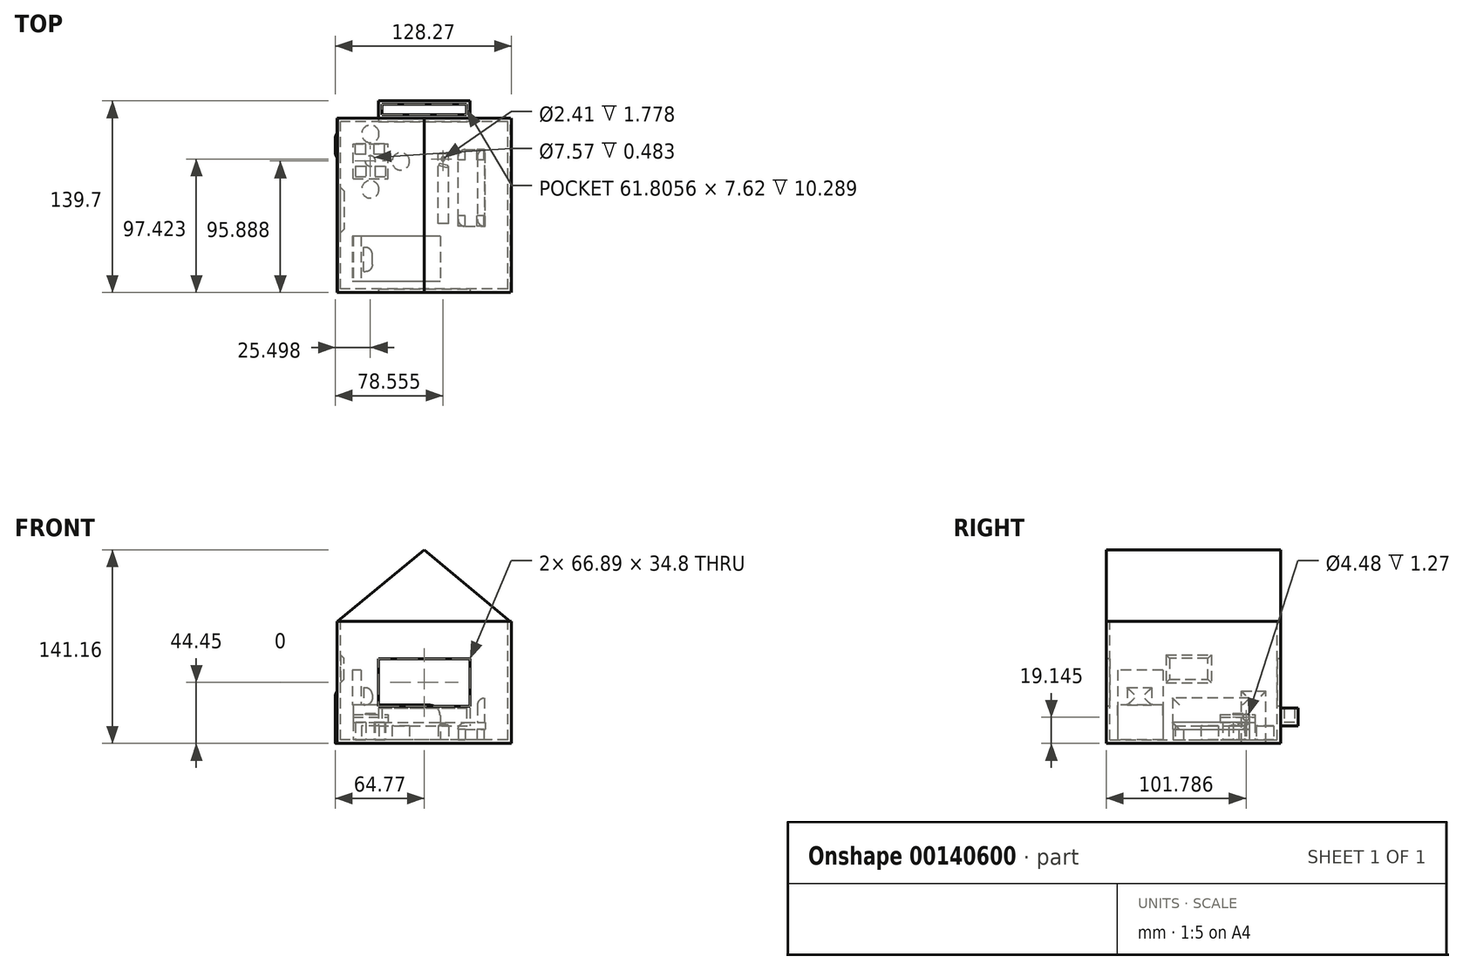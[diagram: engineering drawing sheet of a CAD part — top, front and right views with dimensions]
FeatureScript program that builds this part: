
annotation { "Feature Type Name" : "Feature", "Feature Type Description" : "" }
export const myFeature = defineFeature(function(context is Context, id is Id, definition is map)
    precondition{}
    {
        {
            var Q0;
            Q0=qCreatedBy(makeId("Front.planeOp"),FACE);
            var sketch = newSketch(context, id + "F0", { "sketchPlane" : qUnion([Q0])});
            skLineSegment(sketch, "E0.bottom", {"start": v(63.5, -44.45) * mm, "end": v(-63.5, -44.45) * mm});
            skLineSegment(sketch, "E0.top", {"start": v(63.5, 44.45) * mm, "end": v(-63.5, 44.45) * mm});
            skLineSegment(sketch, "E0.left", {"start": v(63.5, -44.45) * mm, "end": v(63.5, 44.45) * mm});
            skLineSegment(sketch, "E0.right", {"start": v(-63.5, -44.45) * mm, "end": v(-63.5, 44.45) * mm});
            skPoint(sketch, "E0.middle", {"position": v(0, 0) * mm});
            skSolve(sketch);
        }
        {
            var Q0;
            Q0=makeQuery(id+"F0.imprint","IMPRINT",FACE,{"disambiguationData":[TD([[makeQuery(id+"F0.imprint","IMPRINT",EDGE,{"derivedFrom":sQuery(id+"F0.wireOp",EDGE,"E0.bottom")}),-1.0]])]});
            extrude(context, id + "F1", {"entities" : qUnion([Q0]), "depth" : 127 * mm});
        }
        {
            var Q0;
            Q0=makeQuery(id+"F1.opExtrude","SWEPT_FACE",FACE,{"disambiguationData":[OSD([sQuery(id+"F0.wireOp",EDGE,"E0.top")])]});
            shell(context, id + "F2", {"entities" : qUnion([Q0]), "thickness" : 2.54 * mm});
        }
        {
            var Q0;
            Q0=makeQuery(id+"F2.opShell","OFFSET_FACE",FACE,{"disambiguationData":[OSD([sQuery(id+"F0.wireOp",EDGE,"E0.bottom")])]});
            var sketch = newSketch(context, id + "F3", { "sketchPlane" : qUnion([Q0])});
            skLineSegment(sketch, "E1.bottom", {"start": v(-42.46, -26.31) * mm, "end": v(-50.08, -26.31) * mm});
            skLineSegment(sketch, "E1.top", {"start": v(-42.46, -18.7) * mm, "end": v(-50.08, -18.7) * mm});
            skLineSegment(sketch, "E1.left", {"start": v(-42.46, -26.31) * mm, "end": v(-42.46, -18.7) * mm});
            skLineSegment(sketch, "E1.right", {"start": v(-50.08, -26.31) * mm, "end": v(-50.08, -18.7) * mm});
            skPoint(sketch, "E1.middle", {"position": v(-46.27, -22.5) * mm});
            skLineSegment(sketch, "E2.bottom", {"start": v(-28.9, -26.31) * mm, "end": v(-36.51, -26.31) * mm});
            skLineSegment(sketch, "E2.top", {"start": v(-28.9, -18.7) * mm, "end": v(-36.51, -18.7) * mm});
            skLineSegment(sketch, "E2.left", {"start": v(-28.9, -26.31) * mm, "end": v(-28.9, -18.7) * mm});
            skLineSegment(sketch, "E2.right", {"start": v(-36.51, -26.31) * mm, "end": v(-36.51, -18.7) * mm});
            skPoint(sketch, "E2.middle", {"position": v(-32.7, -22.5) * mm});
            skLineSegment(sketch, "E3.bottom", {"start": v(-50.08, -34.68) * mm, "end": v(-42.46, -34.68) * mm});
            skLineSegment(sketch, "E3.top", {"start": v(-50.08, -42.3) * mm, "end": v(-42.46, -42.3) * mm});
            skLineSegment(sketch, "E3.left", {"start": v(-50.08, -34.68) * mm, "end": v(-50.08, -42.3) * mm});
            skLineSegment(sketch, "E3.right", {"start": v(-42.46, -34.68) * mm, "end": v(-42.46, -42.3) * mm});
            skPoint(sketch, "E3.middle", {"position": v(-46.27, -38.5) * mm});
            skLineSegment(sketch, "E4.bottom", {"start": v(-35.96, -34.68) * mm, "end": v(-28.34, -34.68) * mm});
            skLineSegment(sketch, "E4.top", {"start": v(-35.96, -42.3) * mm, "end": v(-28.34, -42.3) * mm});
            skLineSegment(sketch, "E4.left", {"start": v(-35.96, -34.68) * mm, "end": v(-35.96, -42.3) * mm});
            skLineSegment(sketch, "E4.right", {"start": v(-28.34, -34.68) * mm, "end": v(-28.34, -42.3) * mm});
            skPoint(sketch, "E4.middle", {"position": v(-32.15, -38.5) * mm});
            skPoint(sketch, "E4.cornerSnap0", {"position": v(-46.27, -34.68) * mm});
            skSolve(sketch);
        }
        {
            var Q0;
            Q0=makeQuery(id+"F3.imprint","IMPRINT",FACE,{"disambiguationData":[TD([[makeQuery(id+"F3.imprint","IMPRINT",EDGE,{"derivedFrom":sQuery(id+"F3.wireOp",EDGE,"E1.bottom")}),-1.0]])]});
            var Q1;
            Q1=makeQuery(id+"F3.imprint","IMPRINT",FACE,{"disambiguationData":[TD([[makeQuery(id+"F3.imprint","IMPRINT",EDGE,{"derivedFrom":sQuery(id+"F3.wireOp",EDGE,"E2.bottom")}),-1.0]])]});
            var Q2;
            Q2=makeQuery(id+"F3.imprint","IMPRINT",FACE,{"disambiguationData":[TD([[makeQuery(id+"F3.imprint","IMPRINT",EDGE,{"derivedFrom":sQuery(id+"F3.wireOp",EDGE,"E4.bottom")}),-1.0]])]});
            var Q3;
            Q3=makeQuery(id+"F3.imprint","IMPRINT",FACE,{"disambiguationData":[TD([[makeQuery(id+"F3.imprint","IMPRINT",EDGE,{"derivedFrom":sQuery(id+"F3.wireOp",EDGE,"E3.bottom")}),-1.0]])]});
            extrude(context, id + "F4", {"entities" : qUnion([Q0, Q1, Q2, Q3]), "operationType" : NewBodyOperationType.ADD, "depth" : 12.7 * mm});
        }
        {
            var Q0;
            Q0=makeQuery(id+"F4.opExtrude","CAP_FACE",FACE,{"disambiguationData":[OSD([sQuery(id+"F3.wireOp",EDGE,"E1.bottom"),sQuery(id+"F3.wireOp",EDGE,"E1.top"),sQuery(id+"F3.wireOp",EDGE,"E1.left"),sQuery(id+"F3.wireOp",EDGE,"E1.right")])],"isStart":false});
            var sketch = newSketch(context, id + "F5", { "sketchPlane" : qUnion([Q0])});
            skLineSegment(sketch, "E5.bottom", {"start": v(-51.85, -44.1) * mm, "end": v(-26.45, -44.1) * mm});
            skLineSegment(sketch, "E5.top", {"start": v(-51.85, -18.7) * mm, "end": v(-26.45, -18.7) * mm});
            skLineSegment(sketch, "E5.left", {"start": v(-51.85, -44.1) * mm, "end": v(-51.85, -18.7) * mm});
            skLineSegment(sketch, "E5.right", {"start": v(-26.45, -44.1) * mm, "end": v(-26.45, -18.7) * mm});
            skSolve(sketch);
        }
        {
            var Q0;
            Q0 = qSketchRegion(id + "F5", true);
            extrude(context, id + "F6", {"entities" : qUnion([Q0]), "depth" : 3.8 * mm});
        }
        {
            var Q0;
            Q0=makeQuery(id+"F1.opExtrude","CAP_FACE",FACE,{"disambiguationData":[OSD([sQuery(id+"F0.wireOp",EDGE,"E0.bottom"),sQuery(id+"F0.wireOp",EDGE,"E0.top"),sQuery(id+"F0.wireOp",EDGE,"E0.left"),sQuery(id+"F0.wireOp",EDGE,"E0.right")])],"isStart":false});
            var sketch = newSketch(context, id + "F7", { "sketchPlane" : qUnion([Q0])});
            skLineSegment(sketch, "E6.bottom", {"start": v(-33.44, 17.4) * mm, "end": v(33.44, 17.4) * mm});
            skLineSegment(sketch, "E6.top", {"start": v(-33.44, -17.4) * mm, "end": v(33.44, -17.4) * mm});
            skLineSegment(sketch, "E6.left", {"start": v(-33.44, 17.4) * mm, "end": v(-33.44, -17.4) * mm});
            skLineSegment(sketch, "E6.right", {"start": v(33.44, 17.4) * mm, "end": v(33.44, -17.4) * mm});
            skPoint(sketch, "E6.middle", {"position": v(0, 0) * mm});
            skSolve(sketch);
        }
        {
            var Q0;
            Q0 = qSketchRegion(id + "F7", true);
            extrude(context, id + "F8", {"entities" : qUnion([Q0]), "operationType" : NewBodyOperationType.REMOVE, "oppositeDirection" : true, "depth" : 381 * mm});
        }
        {
            var Q0;
            Q0=makeQuery(id+"F1.opExtrude","SWEPT_FACE",FACE,{"disambiguationData":[OSD([sQuery(id+"F0.wireOp",EDGE,"E0.right")])]});
            var sketch = newSketch(context, id + "F9", { "sketchPlane" : qUnion([Q0])});
            skLineSegment(sketch, "E7.bottom", {"start": v(28.62, -44.45) * mm, "end": v(10.84, -44.45) * mm});
            skLineSegment(sketch, "E7.top", {"start": v(28.62, -6.35) * mm, "end": v(10.84, -6.35) * mm});
            skLineSegment(sketch, "E7.left", {"start": v(28.62, -44.45) * mm, "end": v(28.62, -6.35) * mm});
            skLineSegment(sketch, "E7.right", {"start": v(10.84, -44.45) * mm, "end": v(10.84, -6.35) * mm});
            skPoint(sketch, "E7.middle", {"position": v(19.73, -25.4) * mm});
            skCircle(sketch, "E8", {"center": v(25.21, -25.3) * mm, "radius": 2.24 * mm});
            skSolve(sketch);
        }
        {
            var Q0;
            Q0=makeQuery(id+"F9.imprint","IMPRINT",FACE,{"disambiguationData":[TD([[makeQuery(id+"F9.imprint","IMPRINT",EDGE,{"derivedFrom":sQuery(id+"F9.wireOp",EDGE,"E7.bottom")}),-1.0]])]});
            extrude(context, id + "F10", {"entities" : qUnion([Q0]), "operationType" : NewBodyOperationType.ADD, "depth" : 1.27 * mm});
        }
        {
            var Q0;
            Q0=sQuery(id+"F9.wireOp",EDGE,"E8");
            extrude(context, id + "F11", {"bodyType" : ToolBodyType.SURFACE, "surfaceEntities" : qUnion([Q0]), "depth" : 2.03 * mm});
        }
        {
            var Q0;
            Q0=qCreatedBy(makeId("Front.planeOp"),FACE);
            var sketch = newSketch(context, id + "F12", { "sketchPlane" : qUnion([Q0])});
            skLineSegment(sketch, "E9", {"start": v(-63.16, 44.71) * mm, "end": v(0, 96.7) * mm});
            skLineSegment(sketch, "E10", {"start": v(0, 96.7) * mm, "end": v(62.8, 44.28) * mm});
            skLineSegment(sketch, "E11", {"start": v(62.8, 44.28) * mm, "end": v(-63.16, 44.71) * mm});
            skSolve(sketch);
        }
        {
            var Q0;
            Q0=makeQuery(id+"F12.imprint","IMPRINT",FACE,{"disambiguationData":[TD([[makeQuery(id+"F12.imprint","IMPRINT",EDGE,{"derivedFrom":sQuery(id+"F12.wireOp",EDGE,"E9")}),-1.0]])]});
            extrude(context, id + "F13", {"entities" : qUnion([Q0]), "depth" : 127 * mm});
        }
        {
            var Q0;
            Q0=makeQuery(id+"F2.opShell","OFFSET_FACE",FACE,{"disambiguationData":[OSD([sQuery(id+"F0.wireOp",EDGE,"E0.bottom")])]});
            var sketch = newSketch(context, id + "F14", { "sketchPlane" : qUnion([Q0])});
            skLineSegment(sketch, "E12.bottom", {"start": v(29.76, -30.39) * mm, "end": v(24.68, -30.39) * mm});
            skLineSegment(sketch, "E12.top", {"start": v(29.76, -22.77) * mm, "end": v(24.68, -22.77) * mm});
            skLineSegment(sketch, "E12.left", {"start": v(29.76, -30.39) * mm, "end": v(29.76, -22.77) * mm});
            skLineSegment(sketch, "E12.right", {"start": v(24.68, -30.39) * mm, "end": v(24.68, -22.77) * mm});
            skPoint(sketch, "E12.middle", {"position": v(27.22, -26.58) * mm});
            skLineSegment(sketch, "E13.bottom", {"start": v(43.59, -30.39) * mm, "end": v(38.5, -30.39) * mm});
            skLineSegment(sketch, "E13.top", {"start": v(43.59, -22.77) * mm, "end": v(38.5, -22.77) * mm});
            skLineSegment(sketch, "E13.left", {"start": v(43.59, -30.39) * mm, "end": v(43.59, -22.77) * mm});
            skLineSegment(sketch, "E13.right", {"start": v(38.5, -30.39) * mm, "end": v(38.5, -22.77) * mm});
            skPoint(sketch, "E13.middle", {"position": v(41.05, -26.58) * mm});
            skPoint(sketch, "E13.middle.positionSnap0", {"position": v(29.76, -26.58) * mm});
            skPoint(sketch, "E13.centerSnap0", {"position": v(29.76, -26.58) * mm});
            skLineSegment(sketch, "E14.bottom", {"start": v(43.59, -78.48) * mm, "end": v(38.5, -78.48) * mm});
            skLineSegment(sketch, "E14.top", {"start": v(43.59, -70.86) * mm, "end": v(38.5, -70.86) * mm});
            skLineSegment(sketch, "E14.left", {"start": v(43.59, -78.48) * mm, "end": v(43.59, -70.86) * mm});
            skLineSegment(sketch, "E14.right", {"start": v(38.5, -78.48) * mm, "end": v(38.5, -70.86) * mm});
            skPoint(sketch, "E14.middle", {"position": v(41.05, -74.67) * mm});
            skPoint(sketch, "E14.middle.positionSnap0", {"position": v(41.05, -30.39) * mm});
            skPoint(sketch, "E14.centerSnap0", {"position": v(41.05, -30.39) * mm});
            skLineSegment(sketch, "E15.bottom", {"start": v(29.76, -78.48) * mm, "end": v(24.68, -78.48) * mm});
            skLineSegment(sketch, "E15.top", {"start": v(29.76, -70.86) * mm, "end": v(24.68, -70.86) * mm});
            skLineSegment(sketch, "E15.left", {"start": v(29.76, -78.48) * mm, "end": v(29.76, -70.86) * mm});
            skLineSegment(sketch, "E15.right", {"start": v(24.68, -78.48) * mm, "end": v(24.68, -70.86) * mm});
            skPoint(sketch, "E15.middle", {"position": v(27.22, -74.67) * mm});
            skPoint(sketch, "E15.middle.positionSnap0", {"position": v(27.22, -30.39) * mm});
            skPoint(sketch, "E15.middle.positionSnap1", {"position": v(38.5, -74.67) * mm});
            skPoint(sketch, "E15.centerSnap0", {"position": v(27.22, -30.39) * mm});
            skPoint(sketch, "E15.centerSnap1", {"position": v(38.5, -74.67) * mm});
            skSolve(sketch);
        }
        {
            var Q0;
            Q0 = qSketchRegion(id + "F14", true);
            extrude(context, id + "F15", {"entities" : qUnion([Q0]), "operationType" : NewBodyOperationType.ADD, "depth" : 7.62 * mm});
        }
        {
            var Q0;
            Q0=makeQuery(id+"F15.opExtrude","CAP_FACE",FACE,{"disambiguationData":[OSD([sQuery(id+"F14.wireOp",EDGE,"E12.bottom"),sQuery(id+"F14.wireOp",EDGE,"E12.top"),sQuery(id+"F14.wireOp",EDGE,"E12.left"),sQuery(id+"F14.wireOp",EDGE,"E12.right")])],"isStart":false});
            var sketch = newSketch(context, id + "F16", { "sketchPlane" : qUnion([Q0])});
            skLineSegment(sketch, "E16.bottom", {"start": v(24.68, -78.72) * mm, "end": v(44.4, -78.72) * mm});
            skLineSegment(sketch, "E16.top", {"start": v(24.68, -22.77) * mm, "end": v(44.4, -22.77) * mm});
            skLineSegment(sketch, "E16.left", {"start": v(24.68, -78.72) * mm, "end": v(24.68, -22.77) * mm});
            skLineSegment(sketch, "E16.right", {"start": v(44.4, -78.72) * mm, "end": v(44.4, -22.77) * mm});
            skSolve(sketch);
        }
        {
            var Q0;
            Q0 = qSketchRegion(id + "F16", true);
            extrude(context, id + "F17", {"entities" : qUnion([Q0]), "depth" : 5.08 * mm});
        }
        {
            var Q0;
            Q0=makeQuery(id+"F17.opExtrude","CAP_FACE",FACE,{"disambiguationData":[OSD([sQuery(id+"F16.wireOp",EDGE,"E16.bottom"),sQuery(id+"F16.wireOp",EDGE,"E16.top"),sQuery(id+"F16.wireOp",EDGE,"E16.left"),sQuery(id+"F16.wireOp",EDGE,"E16.right")])],"isStart":false});
            var sketch = newSketch(context, id + "F18", { "sketchPlane" : qUnion([Q0])});
            skLineSegment(sketch, "E17.bottom", {"start": v(38.76, -22.77) * mm, "end": v(43.84, -22.77) * mm});
            skLineSegment(sketch, "E17.top", {"start": v(38.76, -78.72) * mm, "end": v(43.84, -78.72) * mm});
            skLineSegment(sketch, "E17.left", {"start": v(38.76, -22.77) * mm, "end": v(38.76, -78.72) * mm});
            skLineSegment(sketch, "E17.right", {"start": v(43.84, -22.77) * mm, "end": v(43.84, -78.72) * mm});
            skPoint(sketch, "E17.middle", {"position": v(41.3, -50.74) * mm});
            skPoint(sketch, "E17.middle.positionSnap0", {"position": v(44.4, -50.74) * mm});
            skPoint(sketch, "E17.centerSnap0", {"position": v(44.4, -50.74) * mm});
            skSolve(sketch);
        }
        {
            var Q0;
            Q0 = qSketchRegion(id + "F18", true);
            extrude(context, id + "F19", {"entities" : qUnion([Q0]), "operationType" : NewBodyOperationType.ADD, "depth" : 17.78 * mm});
        }
        {
            var Q0;
            Q0=makeQuery(id+"F19.opExtrude","SWEPT_EDGE",EDGE,{"disambiguationData":[OSD([sQuery(id+"F16.wireOp",EDGE,"E16.top"),sQuery(id+"F18.wireOp",EDGE,"E17.bottom"),sQuery(id+"F18.wireOp",EDGE,"E17.left")])]});
            var Q1;
            Q1=makeQuery(id+"F19.opExtrude","CAP_EDGE",EDGE,{"disambiguationData":[OSD([sQuery(id+"F18.wireOp",EDGE,"E17.left")])],"isStart":false});
            var Q2;
            Q2=makeQuery(id+"F19.opExtrude","SWEPT_EDGE",EDGE,{"disambiguationData":[OSD([sQuery(id+"F16.wireOp",EDGE,"E16.bottom"),sQuery(id+"F18.wireOp",EDGE,"E17.top"),sQuery(id+"F18.wireOp",EDGE,"E17.left")])]});
            fillet(context, id + "F20", {"entities" : qUnion([Q0, Q1, Q2]), "radius" : 5.08 * mm, "tangentPropagation" : true, "allowEdgeOverflow" : false});
        }
        {
            var Q0;
            Q0=makeQuery(id+"F17.opExtrude","CAP_EDGE",EDGE,{"disambiguationData":[OSD([sQuery(id+"F16.wireOp",EDGE,"E16.left")])],"isStart":false});
            var Q1;
            {var subQ1=sQuery(id+"F16.wireOp",EDGE,"E16.top");Q1=makeQuery(id+"F19.boolean.opBoolean","SPLIT",EDGE,{"disambiguationData":[TD([makeQuery(id+"F15.opExtrude","SWEPT_FACE",FACE,{"disambiguationData":[OSD([sQuery(id+"F14.wireOp",EDGE,"E12.right")])]})])],"derivedFrom":makeQuery(id+"F17.opExtrude","CAP_EDGE",EDGE,{"disambiguationData":[OSD([subQ1])],"isStart":false})});}
            var Q2;
            {var subQ1=sQuery(id+"F16.wireOp",EDGE,"E16.bottom");Q2=makeQuery(id+"F19.boolean.opBoolean","SPLIT",EDGE,{"disambiguationData":[TD([makeQuery(id+"F15.opExtrude","SWEPT_FACE",FACE,{"disambiguationData":[OSD([sQuery(id+"F14.wireOp",EDGE,"E12.right")])]})])],"derivedFrom":makeQuery(id+"F17.opExtrude","CAP_EDGE",EDGE,{"disambiguationData":[OSD([subQ1])],"isStart":false})});}
            var Q3;
            Q3=makeQuery(id+"F17.opExtrude","SWEPT_EDGE",EDGE,{"disambiguationData":[OSD([sQuery(id+"F16.wireOp",EDGE,"E16.bottom"),sQuery(id+"F16.wireOp",EDGE,"E16.left")])]});
            var Q4;
            Q4=makeQuery(id+"F17.boolean.opBoolean","MERGE",EDGE,{"derivedFrom":[makeQuery(id+"F15.opExtrude","SWEPT_EDGE",EDGE,{"disambiguationData":[OSD([sQuery(id+"F14.wireOp",EDGE,"E12.top"),sQuery(id+"F14.wireOp",EDGE,"E12.right")])]}),makeQuery(id+"F17.opExtrude","SWEPT_EDGE",EDGE,{"disambiguationData":[OSD([sQuery(id+"F16.wireOp",EDGE,"E16.top"),sQuery(id+"F16.wireOp",EDGE,"E16.left")])]})]});
            fillet(context, id + "F21", {"entities" : qUnion([Q0, Q1, Q2, Q3, Q4]), "radius" : 5.08 * mm, "tangentPropagation" : true, "allowEdgeOverflow" : false});
        }
        {
            var Q0;
            Q0=makeQuery(id+"F2.opShell","OFFSET_FACE",FACE,{"disambiguationData":[OSD([sQuery(id+"F0.wireOp",EDGE,"E0.right")])]});
            var sketch = newSketch(context, id + "F22", { "sketchPlane" : qUnion([Q0])});
            skLineSegment(sketch, "E18.bottom", {"start": v(-47.96, -2.83) * mm, "end": v(-86.06, -2.83) * mm});
            skLineSegment(sketch, "E18.top", {"start": v(-47.96, 22.57) * mm, "end": v(-86.06, 22.57) * mm});
            skLineSegment(sketch, "E18.left", {"start": v(-47.96, -2.83) * mm, "end": v(-47.96, 22.57) * mm});
            skLineSegment(sketch, "E18.right", {"start": v(-86.06, -2.83) * mm, "end": v(-86.06, 22.57) * mm});
            skPoint(sketch, "E18.middle", {"position": v(-67, 9.87) * mm});
            skSolve(sketch);
        }
        {
            var Q0;
            Q0 = qSketchRegion(id + "F22", true);
            extrude(context, id + "F23", {"entities" : qUnion([Q0]), "depth" : 2.54 * mm});
        }
        {
            var Q0;
            Q0=makeQuery(id+"F23.opExtrude","CAP_EDGE",EDGE,{"disambiguationData":[OSD([sQuery(id+"F22.wireOp",EDGE,"E18.top")])],"isStart":false});
            var Q1;
            Q1=makeQuery(id+"F23.opExtrude","CAP_EDGE",EDGE,{"disambiguationData":[OSD([sQuery(id+"F22.wireOp",EDGE,"E18.right")])],"isStart":false});
            var Q2;
            Q2=makeQuery(id+"F23.opExtrude","CAP_EDGE",EDGE,{"disambiguationData":[OSD([sQuery(id+"F22.wireOp",EDGE,"E18.left")])],"isStart":false});
            var Q3;
            Q3=makeQuery(id+"F23.opExtrude","CAP_FACE",FACE,{"disambiguationData":[OSD([sQuery(id+"F22.wireOp",EDGE,"E18.bottom"),sQuery(id+"F22.wireOp",EDGE,"E18.top"),sQuery(id+"F22.wireOp",EDGE,"E18.left"),sQuery(id+"F22.wireOp",EDGE,"E18.right")])],"isStart":false});
            chamfer(context, id + "F24", {"entities" : qUnion([Q0, Q1, Q2, Q3]), "width" : 5.08 * mm, "tangentPropagation" : true});
        }
        {
            var Q0;
            Q0=makeQuery(id+"F2.opShell","OFFSET_FACE",FACE,{"disambiguationData":[OSD([sQuery(id+"F0.wireOp",EDGE,"E0.bottom")])]});
            var sketch = newSketch(context, id + "F25", { "sketchPlane" : qUnion([Q0])});
            skLineSegment(sketch, "E19.bottom", {"start": v(11.6, -85.89) * mm, "end": v(-51.9, -85.89) * mm});
            skLineSegment(sketch, "E19.top", {"start": v(11.6, -118.9) * mm, "end": v(-51.9, -118.9) * mm});
            skLineSegment(sketch, "E19.left", {"start": v(11.6, -85.89) * mm, "end": v(11.6, -118.9) * mm});
            skLineSegment(sketch, "E19.right", {"start": v(-51.9, -85.89) * mm, "end": v(-51.9, -118.9) * mm});
            skPoint(sketch, "E19.middle", {"position": v(-20.16, -102.4) * mm});
            skSolve(sketch);
        }
        {
            var Q0;
            Q0 = qSketchRegion(id + "F25", true);
            extrude(context, id + "F26", {"entities" : qUnion([Q0]), "depth" : 25.4 * mm});
        }
        {
            var Q0;
            Q0=makeQuery(id+"F26.opExtrude","CAP_FACE",FACE,{"disambiguationData":[OSD([sQuery(id+"F25.wireOp",EDGE,"E19.bottom"),sQuery(id+"F25.wireOp",EDGE,"E19.top"),sQuery(id+"F25.wireOp",EDGE,"E19.left"),sQuery(id+"F25.wireOp",EDGE,"E19.right")])],"isStart":false});
            var sketch = newSketch(context, id + "F27", { "sketchPlane" : qUnion([Q0])});
            skLineSegment(sketch, "E20.bottom", {"start": v(-46.08, -85.89) * mm, "end": v(-52.43, -85.89) * mm});
            skLineSegment(sketch, "E20.top", {"start": v(-46.08, -118.9) * mm, "end": v(-52.43, -118.9) * mm});
            skLineSegment(sketch, "E20.left", {"start": v(-46.08, -85.89) * mm, "end": v(-46.08, -118.9) * mm});
            skLineSegment(sketch, "E20.right", {"start": v(-52.43, -85.89) * mm, "end": v(-52.43, -118.9) * mm});
            skPoint(sketch, "E20.middle", {"position": v(-49.26, -102.4) * mm});
            skSolve(sketch);
        }
        {
            var Q0;
            Q0 = qSketchRegion(id + "F27", true);
            extrude(context, id + "F28", {"entities" : qUnion([Q0]), "depth" : 25.4 * mm});
        }
        {
            var Q0;
            Q0=makeQuery(id+"F26.opExtrude","CAP_FACE",FACE,{"disambiguationData":[OSD([sQuery(id+"F25.wireOp",EDGE,"E19.bottom"),sQuery(id+"F25.wireOp",EDGE,"E19.top"),sQuery(id+"F25.wireOp",EDGE,"E19.left"),sQuery(id+"F25.wireOp",EDGE,"E19.right")])],"isStart":false});
            var sketch = newSketch(context, id + "F29", { "sketchPlane" : qUnion([Q0])});
            skLineSegment(sketch, "E21.bottom", {"start": v(-44.22, -111.8) * mm, "end": v(-37.87, -111.8) * mm});
            skLineSegment(sketch, "E21.top", {"start": v(-44.22, -94.02) * mm, "end": v(-37.87, -94.02) * mm});
            skLineSegment(sketch, "E21.left", {"start": v(-44.22, -111.8) * mm, "end": v(-44.22, -94.02) * mm});
            skLineSegment(sketch, "E21.right", {"start": v(-37.87, -111.8) * mm, "end": v(-37.87, -94.02) * mm});
            skSolve(sketch);
        }
        {
            var Q0;
            Q0 = qSketchRegion(id + "F29", true);
            extrude(context, id + "F30", {"entities" : qUnion([Q0]), "depth" : 12.7 * mm});
        }
        {
            var Q0;
            Q0=makeQuery(id+"F30.opExtrude","CAP_EDGE",EDGE,{"disambiguationData":[OSD([sQuery(id+"F29.wireOp",EDGE,"E21.right")])],"isStart":false});
            var Q1;
            Q1=makeQuery(id+"F30.opExtrude","SWEPT_EDGE",EDGE,{"disambiguationData":[OSD([sQuery(id+"F29.wireOp",EDGE,"E21.top"),sQuery(id+"F29.wireOp",EDGE,"E21.right")])]});
            var Q2;
            Q2=makeQuery(id+"F30.opExtrude","SWEPT_EDGE",EDGE,{"disambiguationData":[OSD([sQuery(id+"F29.wireOp",EDGE,"E21.bottom"),sQuery(id+"F29.wireOp",EDGE,"E21.right")])]});
            var Q3;
            Q3=makeQuery(id+"F30.opExtrude","SWEPT_FACE",FACE,{"disambiguationData":[OSD([sQuery(id+"F29.wireOp",EDGE,"E21.right")])]});
            fillet(context, id + "F31", {"entities" : qUnion([Q0, Q1, Q2, Q3]), "radius" : 5.08 * mm, "tangentPropagation" : true, "allowEdgeOverflow" : false});
        }
        {
            var Q0;
            Q0=makeQuery(id+"F10.opExtrude","CAP_EDGE",EDGE,{"disambiguationData":[OSD([sQuery(id+"F9.wireOp",EDGE,"E7.top")])],"isStart":false});
            var Q1;
            Q1=makeQuery(id+"F10.opExtrude","CAP_EDGE",EDGE,{"disambiguationData":[OSD([sQuery(id+"F9.wireOp",EDGE,"E7.left")])],"isStart":false});
            var Q2;
            Q2=makeQuery(id+"F10.opExtrude","CAP_EDGE",EDGE,{"disambiguationData":[OSD([sQuery(id+"F9.wireOp",EDGE,"E7.right")])],"isStart":false});
            fillet(context, id + "F32", {"entities" : qUnion([Q0, Q1, Q2]), "radius" : 5.08 * mm, "tangentPropagation" : true, "allowEdgeOverflow" : false});
        }
        {
            var Q0;
            Q0=makeQuery(id+"F2.opShell","OFFSET_FACE",FACE,{"disambiguationData":[OSD([sQuery(id+"F0.wireOp",EDGE,"E0.bottom")])]});
            var sketch = newSketch(context, id + "F33", { "sketchPlane" : qUnion([Q0])});
            skCircle(sketch, "E22", {"center": v(-17.13, -31.38) * mm, "radius": 6.35 * mm});
            skCircle(sketch, "E23", {"center": v(-39.25, -11.33) * mm, "radius": 6.35 * mm});
            skCircle(sketch, "E24", {"center": v(-39.3, -51.8) * mm, "radius": 6.35 * mm});
            skSolve(sketch);
        }
        {
            var Q0;
            Q0 = qSketchRegion(id + "F33", true);
            extrude(context, id + "F34", {"entities" : qUnion([Q0]), "depth" : 10.16 * mm});
        }
        {
            var Q0;
            Q0=makeQuery(id+"F2.opShell","OFFSET_FACE",FACE,{"disambiguationData":[OSD([sQuery(id+"F0.wireOp",EDGE,"E0.bottom")])]});
            var sketch = newSketch(context, id + "F35", { "sketchPlane" : qUnion([Q0])});
            skLineSegment(sketch, "E25.bottom", {"start": v(17.73, -76.8) * mm, "end": v(10.1, -76.8) * mm});
            skLineSegment(sketch, "E25.top", {"start": v(17.73, -26) * mm, "end": v(10.1, -26) * mm});
            skLineSegment(sketch, "E25.left", {"start": v(17.73, -76.8) * mm, "end": v(17.73, -26) * mm});
            skLineSegment(sketch, "E25.right", {"start": v(10.1, -76.8) * mm, "end": v(10.1, -26) * mm});
            skPoint(sketch, "E25.middle", {"position": v(13.92, -51.4) * mm});
            skSolve(sketch);
        }
        {
            var Q0;
            Q0 = qSketchRegion(id + "F35", true);
            extrude(context, id + "F36", {"entities" : qUnion([Q0]), "depth" : 10.16 * mm});
        }
        {
            var Q0;
            Q0=makeQuery(id+"F26.opExtrude","CAP_EDGE",EDGE,{"disambiguationData":[OSD([sQuery(id+"F25.wireOp",EDGE,"E19.left")])],"isStart":false});
            fillet(context, id + "F37", {"entities" : qUnion([Q0]), "radius" : 7.62 * mm, "tangentPropagation" : true, "allowEdgeOverflow" : false});
        }
        {
            var Q0;
            Q0=makeQuery(id+"F36.opExtrude","CAP_FACE",FACE,{"disambiguationData":[OSD([sQuery(id+"F35.wireOp",EDGE,"E25.bottom"),sQuery(id+"F35.wireOp",EDGE,"E25.top"),sQuery(id+"F35.wireOp",EDGE,"E25.left"),sQuery(id+"F35.wireOp",EDGE,"E25.right")])],"isStart":false});
            var sketch = newSketch(context, id + "F38", { "sketchPlane" : qUnion([Q0])});
            skCircle(sketch, "E26", {"center": v(13.78, -29.58) * mm, "radius": 1.46 * mm});
            skSolve(sketch);
        }
        {
            var Q0;
            Q0 = qSketchRegion(id + "F38", true);
            var Q1;
            Q1=makeQuery(id+"F6.opExtrude","CAP_FACE",FACE,{"disambiguationData":[OSD([sQuery(id+"F5.wireOp",EDGE,"E5.bottom"),sQuery(id+"F5.wireOp",EDGE,"E5.top"),sQuery(id+"F5.wireOp",EDGE,"E5.left"),sQuery(id+"F5.wireOp",EDGE,"E5.right")])],"isStart":false});
            extrude(context, id + "F39", {"entities" : qUnion([Q0, Q1]), "depth" : 2.03 * mm});
        }
        {
            var Q0;
            Q0=makeQuery(id+"F39.opExtrude","CAP_FACE",FACE,{"disambiguationData":[OSD([sQuery(id+"F38.wireOp",EDGE,"E26")])],"isStart":false});
            shell(context, id + "F40", {"entities" : qUnion([Q0]), "thickness" : 0.25 * mm});
        }
        {
            var Q0;
            Q0=makeQuery(id+"F39.opExtrude","CAP_FACE",FACE,{"disambiguationData":[OSD([sQuery(id+"F5.wireOp",EDGE,"E5.bottom"),sQuery(id+"F5.wireOp",EDGE,"E5.top"),sQuery(id+"F5.wireOp",EDGE,"E5.left"),sQuery(id+"F5.wireOp",EDGE,"E5.right")])],"isStart":false});
            var sketch = newSketch(context, id + "F41", { "sketchPlane" : qUnion([Q0])});
            skCircle(sketch, "E27", {"center": v(-39.27, -31.11) * mm, "radius": 3.81 * mm});
            skSolve(sketch);
        }
        {
            var Q0;
            Q0 = qSketchRegion(id + "F41", true);
            extrude(context, id + "F42", {"entities" : qUnion([Q0]), "depth" : 0.5 * mm});
        }
        {
            var Q0;
            Q0=makeQuery(id+"F42.opExtrude","CAP_FACE",FACE,{"disambiguationData":[OSD([sQuery(id+"F41.wireOp",EDGE,"E27")])],"isStart":false});
            shell(context, id + "F43", {"entities" : qUnion([Q0]), "thickness" : 0.03 * mm});
        }
        {
            var Q0;
            Q0=makeQuery(id+"F36.opExtrude","CAP_FACE",FACE,{"disambiguationData":[OSD([sQuery(id+"F35.wireOp",EDGE,"E25.bottom"),sQuery(id+"F35.wireOp",EDGE,"E25.top"),sQuery(id+"F35.wireOp",EDGE,"E25.left"),sQuery(id+"F35.wireOp",EDGE,"E25.right")])],"isStart":false});
            var sketch = newSketch(context, id + "F44", { "sketchPlane" : qUnion([Q0])});
            skLineSegment(sketch, "E28.bottom", {"start": v(16.9, -36.2) * mm, "end": v(10.7, -34.54) * mm});
            skLineSegment(sketch, "E28.top", {"start": v(17.38, -34.43) * mm, "end": v(11.17, -32.77) * mm});
            skLineSegment(sketch, "E28.left", {"start": v(16.9, -36.2) * mm, "end": v(17.38, -34.43) * mm});
            skLineSegment(sketch, "E28.right", {"start": v(10.7, -34.54) * mm, "end": v(11.17, -32.77) * mm});
            skPoint(sketch, "E28.middle", {"position": v(13.53, -34.11) * mm});
            skSolve(sketch);
        }
        {
            var Q0;
            Q0 = qSketchRegion(id + "F44", true);
            extrude(context, id + "F45", {"entities" : qUnion([Q0]), "depth" : 0.76 * mm});
        }
        {
            var Q0;
            Q0=makeQuery(id+"F1.opExtrude","CAP_FACE",FACE,{"disambiguationData":[OSD([sQuery(id+"F0.wireOp",EDGE,"E0.bottom"),sQuery(id+"F0.wireOp",EDGE,"E0.top"),sQuery(id+"F0.wireOp",EDGE,"E0.left"),sQuery(id+"F0.wireOp",EDGE,"E0.right")])],"isStart":true});
            var sketch = newSketch(context, id + "F46", { "sketchPlane" : qUnion([Q0])});
            skLineSegment(sketch, "E29.bottom", {"start": v(33.44, -18.7) * mm, "end": v(-33.44, -18.7) * mm});
            skLineSegment(sketch, "E29.top", {"start": v(33.44, -31.54) * mm, "end": v(-33.44, -31.54) * mm});
            skLineSegment(sketch, "E29.left", {"start": v(33.44, -18.7) * mm, "end": v(33.44, -31.54) * mm});
            skLineSegment(sketch, "E29.right", {"start": v(-33.44, -18.7) * mm, "end": v(-33.44, -31.54) * mm});
            skPoint(sketch, "E29.middle", {"position": v(0, -25.12) * mm});
            skSolve(sketch);
        }
        {
            var Q0;
            Q0 = qSketchRegion(id + "F46", true);
            extrude(context, id + "F47", {"entities" : qUnion([Q0]), "depth" : 12.7 * mm});
        }
        {
            var Q0;
            Q0=makeQuery(id+"F47.opExtrude","SWEPT_FACE",FACE,{"disambiguationData":[OSD([sQuery(id+"F46.wireOp",EDGE,"E29.bottom")])]});
            shell(context, id + "F48", {"entities" : qUnion([Q0]), "thickness" : 2.54 * mm});
        }
    });
